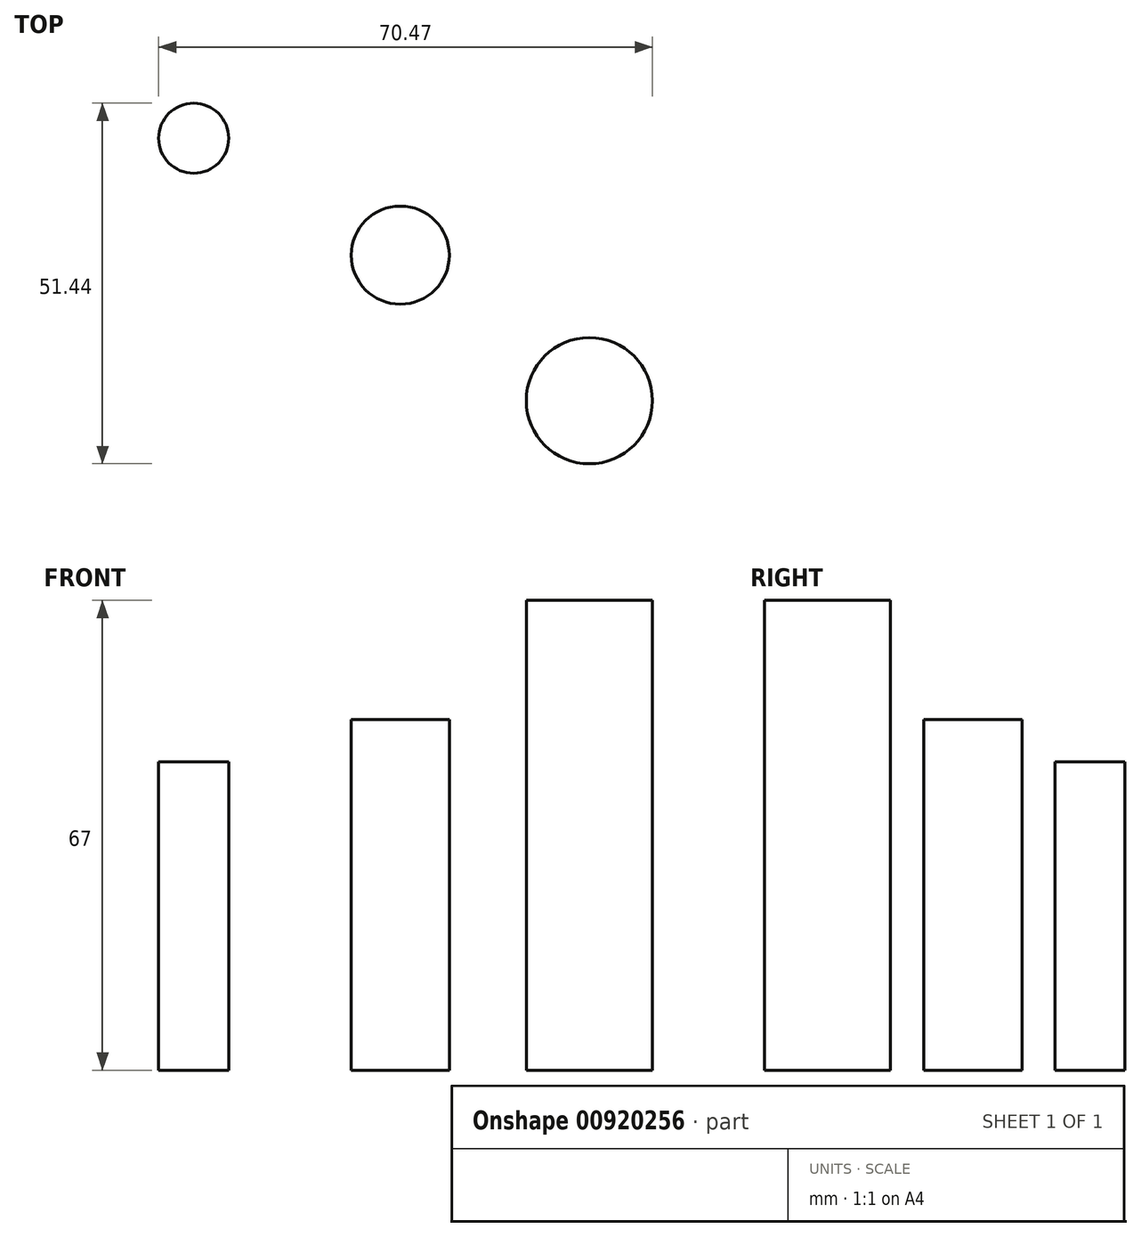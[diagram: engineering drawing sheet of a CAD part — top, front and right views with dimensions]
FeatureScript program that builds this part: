
annotation { "Feature Type Name" : "Feature", "Feature Type Description" : "" }
export const myFeature = defineFeature(function(context is Context, id is Id, definition is map)
    precondition{}
    {
        {
            var Q0;
            Q0=qCreatedBy(makeId("Top.planeOp"),FACE);
            var sketch = newSketch(context, id + "F0", { "sketchPlane" : qUnion([Q0])});
            skCircle(sketch, "E0", {"center": v(0, 0) * mm, "radius": 9 * mm});
            skSolve(sketch);
        }
        {
            var Q0;
            Q0 = qSketchRegion(id + "F0", true);
            extrude(context, id + "F1", {"entities" : qUnion([Q0]), "depth" : 67 * mm, "offsetDistance" : 25 * mm});
        }
        {
            var Q0;
            Q0=qCreatedBy(makeId("Top.planeOp"),FACE);
            var sketch = newSketch(context, id + "F2", { "sketchPlane" : qUnion([Q0])});
            skCircle(sketch, "E1", {"center": v(-26.98, 20.76) * mm, "radius": 7 * mm});
            skSolve(sketch);
        }
        {
            var Q0;
            Q0 = qSketchRegion(id + "F2", true);
            extrude(context, id + "F3", {"entities" : qUnion([Q0]), "depth" : 50 * mm, "offsetDistance" : 25 * mm});
        }
        {
            var Q0;
            Q0=qCreatedBy(makeId("Top.planeOp"),FACE);
            var sketch = newSketch(context, id + "F4", { "sketchPlane" : qUnion([Q0])});
            skCircle(sketch, "E2", {"center": v(-56.47, 37.44) * mm, "radius": 5 * mm});
            skSolve(sketch);
        }
        {
            var Q0;
            Q0 = qSketchRegion(id + "F4", true);
            extrude(context, id + "F5", {"entities" : qUnion([Q0]), "depth" : 44 * mm, "offsetDistance" : 25 * mm});
        }
    });
